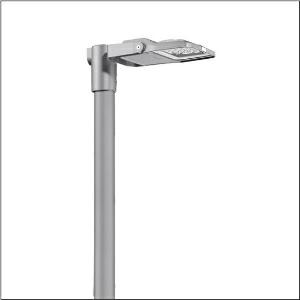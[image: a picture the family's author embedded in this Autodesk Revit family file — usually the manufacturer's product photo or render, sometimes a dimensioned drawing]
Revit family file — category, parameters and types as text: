
# Revit family: floodlight_fl_21_iq_micro___pl61_5xa7762a4c3a_196d
name_source: partatom
category: Lighting Fixtures
units: mm (PartAtom-declared; Revit-internal decimal feet)

## family parameters
Cut with Voids When Loaded = No
Host = Face
Light Source = No
Part Type = Normal
Room Calculation Point = No
Round Connector Dimension = Use Diameter
Shared = No

## types (1)
- --- (1 x LED, 3030 lm, 23.1 W, 4000K)
    Apparent Load = 23 VA
    CIE Flux Codes = 33 65 98 100 100
    Color Rendering = 70
    Color Temperature = 4000K
    Default Elevation = 1800 mm
    Description = Floodlight FL 21 iQ micro, floodlight, primary light control with lens, of PMMA, primary optical cover: protective disc, of toughened safety glass, transparent, light distribution: PL61, light emission: direct distribution, installation type: surface-mounted, LED, High Power LED, rated luminous flux: 3.030lm, luminous efficacy: 131lm/W, light colour: 740, colour temperature: 4000K, control: Auto-Match, Temp-Guard, Night-Set, Smart-Wire, Desk-Remote (wireless, voltage-free reading and setting of iQ features in the workshop via application-optimized NFC function/RFID function), optimised constant luminous flux control (CLO 2.0), Street-Remote, with terminal, 6-pole, mains connection: 220..240V, AC, 50/60Hz, start of lifetime: 23W, end of service life: 24W, reduction: 11W, luminaire housing, of diecast aluminium, powder-coated, Siteco® metallic grey (DB 702S), corrosivity category C5 mid according to DIN EN ISO 12944, sealing non-destructively replaceable, please order mast flange separately, mast bracket, of steel, galvanised, powder-coated, Siteco® metallic grey (DB 702S), protection rating (complete): IP66, insulation class (complete): insulation class II (safety insulation), certification: CE, ENEC, VDE, protection symbol: D, impact resistance: IK07, permissible operating ambient temperature: -40..+40°C, permissible operating ambient temperature for outdoor applications: -40..+50°C, standard: DIN EN 12944, LABS conformity tested according to VDMA 24364:2018-05, packaging unit: 1 piece

Light Distribution: PL61
    Height = 65 mm
    Lamp = 1 x LED
    Lamp Light Flux = 3030 lm
    Lamp Power = 23.1 W
    Lamp count = 1
    Length = 312 mm
    Luminous efficacy = 131 lm/W
    Manufacturer = Siteco
    ModVariant = No
    Model = 5XA7762A4C3A
    Number of Poles = 1
    OnlyDefault = Yes
    Power Factor = 1
    Product Name = Floodlight FL 21 iQ micro | PL61
    Product group = floodlight | pylon annexe
    ProductGroupID = 6200
    Protection Class = Protection class II
    Protection Degree = IP 66
    RLX_Detail_Level = 1
    RLX_Emergency_Light_Flux = 0 lm
    RLX_Emergency_Type = 0
    RLX_Emergency_Type_DB = No
    RlxData = <blob elided: 101877 chars, md5=3d8c2f65>
    Socket = socket
    Standby Power = 0 W
    System Light Flux = 3030 lm
    System Power = 23 W
    Type Comments = factory setting: luminous flux: 100 % | dim-lin: 254 | 455 mA
    Type Image = l_1007121.jpg
    URL = http://relux.com
    VarID = @adj_146905
    Voltage = 0 V
    Weight = 0.00 kg
    Width = 230 mm

## geometry (parser evidence)
native form markers: Blend x4, Sweep x14
no freeform markers — native parametric forms only
